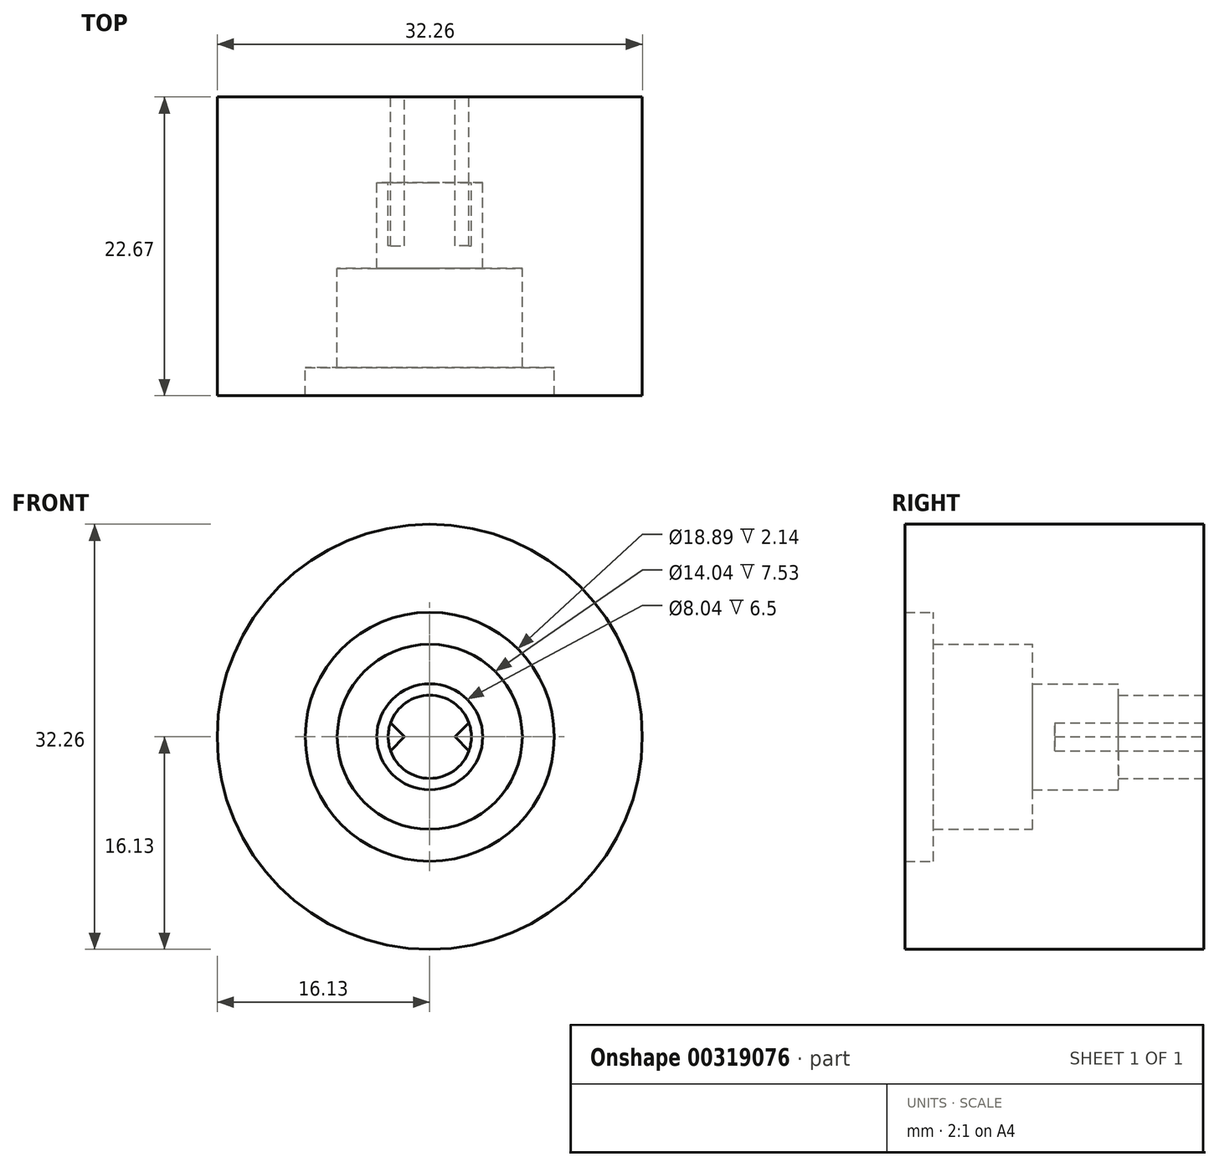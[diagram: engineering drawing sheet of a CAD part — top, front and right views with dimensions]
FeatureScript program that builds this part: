
annotation { "Feature Type Name" : "Feature", "Feature Type Description" : "" }
export const myFeature = defineFeature(function(context is Context, id is Id, definition is map)
    precondition{}
    {
        {
            var Q0;
            Q0=qCreatedBy(makeId("Front.planeOp"),FACE);
            var sketch = newSketch(context, id + "F0", { "sketchPlane" : qUnion([Q0])});
            skCircle(sketch, "E0", {"center": v(0, 0) * mm, "radius": 16.12 * mm});
            skCircle(sketch, "E1", {"center": v(0, 0) * mm, "radius": 4.02 * mm});
            skCircle(sketch, "E2", {"center": v(0, 0) * mm, "radius": 3.15 * mm});
            skCircle(sketch, "E3", {"center": v(0, 0) * mm, "radius": 7.02 * mm});
            skCircle(sketch, "E4", {"center": v(0, 0) * mm, "radius": 9.45 * mm});
            skLineSegment(sketch, "E5", {"start": v(2.97, 1.06) * mm, "end": v(1.91, 0) * mm});
            skLineSegment(sketch, "E6", {"start": v(1.91, 0) * mm, "end": v(2.97, -1.06) * mm});
            skLineSegment(sketch, "E7", {"start": v(-2.97, 1.06) * mm, "end": v(-1.91, 0) * mm});
            skLineSegment(sketch, "E8", {"start": v(-1.91, 0) * mm, "end": v(-2.97, -1.06) * mm});
            skSolve(sketch);
        }
        {
            var Q0;
            Q0 = qSketchRegion(id + "F0", true);
            extrude(context, id + "F1", {"entities" : qUnion([Q0]), "depth" : 22.67 * mm});
        }
        {
            var Q0;
            Q0=makeQuery(id+"F0.imprint","IMPRINT",FACE,{"disambiguationData":[TD([[makeQuery(id+"F0.imprint","IMPRINT",EDGE,{"derivedFrom":sQuery(id+"F0.wireOp",EDGE,"E3")}),-1.0]])]});
            var sketch = newSketch(context, id + "F2", { "sketchPlane" : qUnion([Q0])});
            skSolve(sketch);
        }
        {
            var Q0;
            Q0 = qSketchRegion(id + "F2", true);
            var Q1;
            Q1=makeQuery(id+"F0.imprint","IMPRINT",FACE,{"disambiguationData":[TD([[makeQuery(id+"F0.imprint","IMPRINT",EDGE,{"derivedFrom":sQuery(id+"F0.wireOp",EDGE,"E3")}),-1.0]])]});
            extrude(context, id + "F3", {"entities" : qUnion([Q0, Q1]), "operationType" : NewBodyOperationType.ADD, "depth" : 20.53 * mm});
        }
        {
            var Q0;
            Q0=makeQuery(id+"F0.imprint","IMPRINT",FACE,{"disambiguationData":[TD([[makeQuery(id+"F0.imprint","IMPRINT",EDGE,{"derivedFrom":sQuery(id+"F0.wireOp",EDGE,"E3")}),1.0]])]});
            var sketch = newSketch(context, id + "F4", { "sketchPlane" : qUnion([Q0])});
            skSolve(sketch);
        }
        {
            var Q0;
            Q0 = qSketchRegion(id + "F4", true);
            var Q1;
            Q1=makeQuery(id+"F0.imprint","IMPRINT",FACE,{"disambiguationData":[TD([[makeQuery(id+"F0.imprint","IMPRINT",EDGE,{"derivedFrom":sQuery(id+"F0.wireOp",EDGE,"E3")}),1.0]])]});
            extrude(context, id + "F5", {"entities" : qUnion([Q0, Q1]), "operationType" : NewBodyOperationType.ADD, "depth" : 13 * mm});
        }
        {
            var Q0;
            Q0=makeQuery(id+"F0.imprint","IMPRINT",FACE,{"disambiguationData":[TD([[makeQuery(id+"F0.imprint","IMPRINT",EDGE,{"derivedFrom":sQuery(id+"F0.wireOp",EDGE,"E2")}),-1.0]])]});
            extrude(context, id + "F6", {"entities" : qUnion([Q0]), "operationType" : NewBodyOperationType.ADD, "depth" : 6.5 * mm});
        }
        {
            var Q0;
            Q0=makeQuery(id+"F0.imprint","IMPRINT",FACE,{"disambiguationData":[TD([[makeQuery(id+"F0.imprint","IMPRINT",EDGE,{"derivedFrom":sQuery(id+"F0.wireOp",EDGE,"E0")}),1.0]])]});
            var Q1;
            {var subQ0=sQuery(id+"F0.wireOp",EDGE,"E7");Q1=makeQuery(id+"F0.imprint","IMPRINT",FACE,{"disambiguationData":[TD([[makeQuery(id+"F0.imprint","IMPRINT",EDGE,{"derivedFrom":subQ0}),-1.0]])]});}
            var Q2;
            {var subQ0=sQuery(id+"F0.wireOp",EDGE,"E5");Q2=makeQuery(id+"F0.imprint","IMPRINT",FACE,{"disambiguationData":[TD([[makeQuery(id+"F0.imprint","IMPRINT",EDGE,{"derivedFrom":subQ0}),1.0]])]});}
            extrude(context, id + "F7", {"entities" : qUnion([Q0, Q1, Q2]), "operationType" : NewBodyOperationType.ADD, "depth" : 11.3 * mm});
        }
    });
